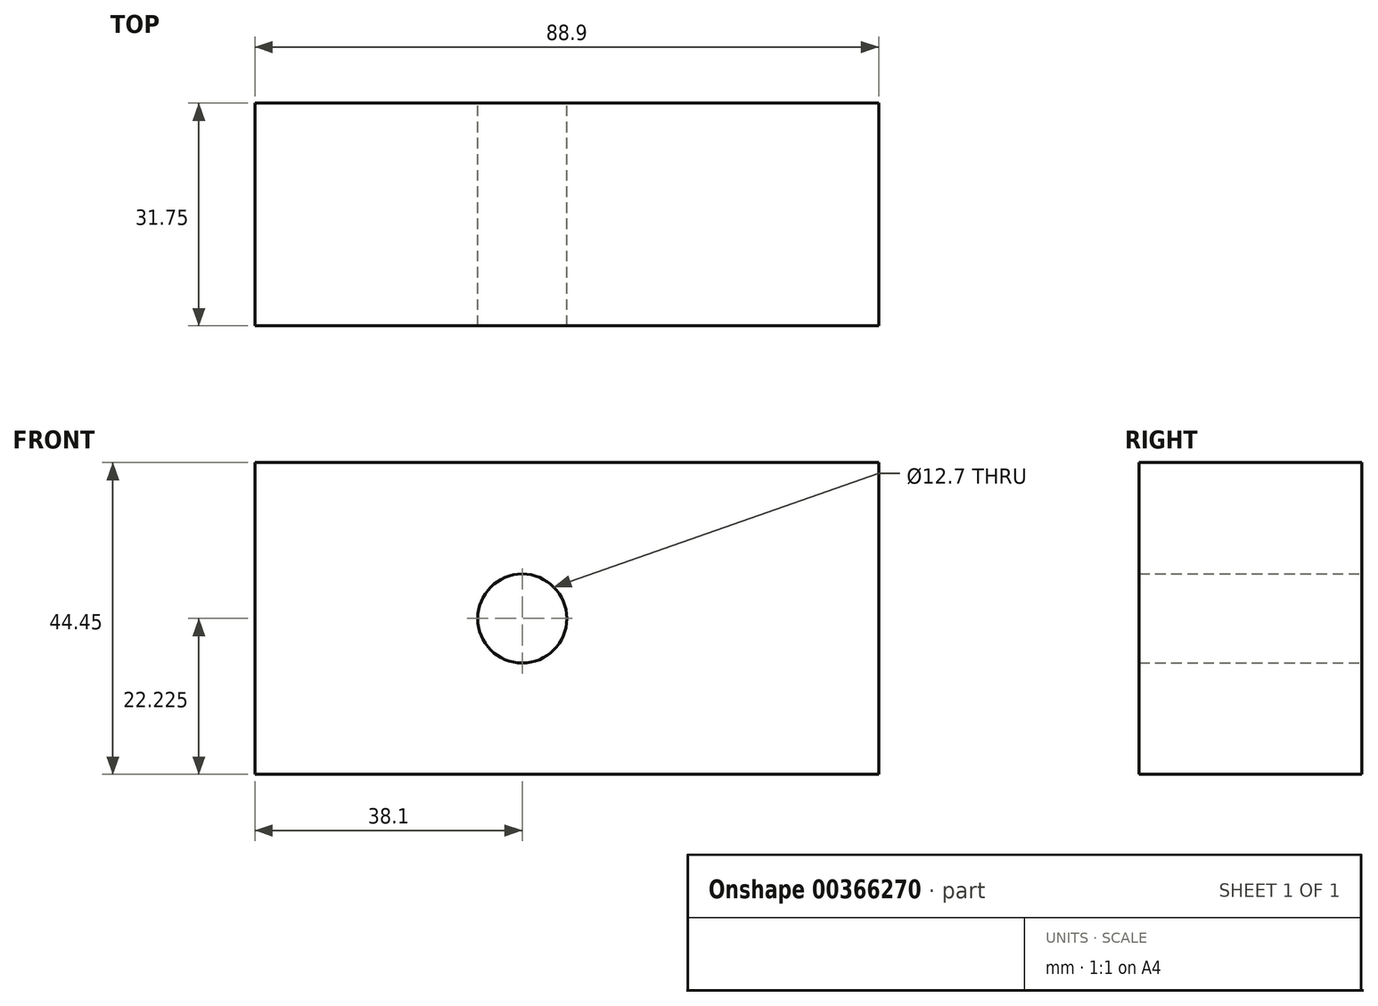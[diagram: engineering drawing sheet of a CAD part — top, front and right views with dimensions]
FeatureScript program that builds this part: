
annotation { "Feature Type Name" : "Feature", "Feature Type Description" : "" }
export const myFeature = defineFeature(function(context is Context, id is Id, definition is map)
    precondition{}
    {
        {
            var Q0;
            Q0=qCreatedBy(makeId("Front.planeOp"),FACE);
            var sketch = newSketch(context, id + "F0", { "sketchPlane" : qUnion([Q0])});
            skLineSegment(sketch, "E0", {"start": v(0, 0) * mm, "end": v(88.9, 0) * mm});
            skLineSegment(sketch, "E1", {"start": v(88.9, 0) * mm, "end": v(88.9, 44.45) * mm});
            skLineSegment(sketch, "E2", {"start": v(88.9, 44.45) * mm, "end": v(0, 44.45) * mm});
            skLineSegment(sketch, "E3", {"start": v(0, 44.45) * mm, "end": v(0, 0) * mm});
            skCircle(sketch, "E4", {"center": v(38.1, 22.22) * mm, "radius": 6.35 * mm});
            skPoint(sketch, "E4.centerSnap0", {"position": v(0, 22.23) * mm});
            skSolve(sketch);
        }
        {
            var Q0;
            Q0=makeQuery(id+"F0.imprint","IMPRINT",FACE,{"disambiguationData":[TD([[makeQuery(id+"F0.imprint","IMPRINT",EDGE,{"derivedFrom":sQuery(id+"F0.wireOp",EDGE,"E0")}),1.0]])]});
            extrude(context, id + "F1", {"entities" : qUnion([Q0]), "depth" : 31.75 * mm});
        }
    });
